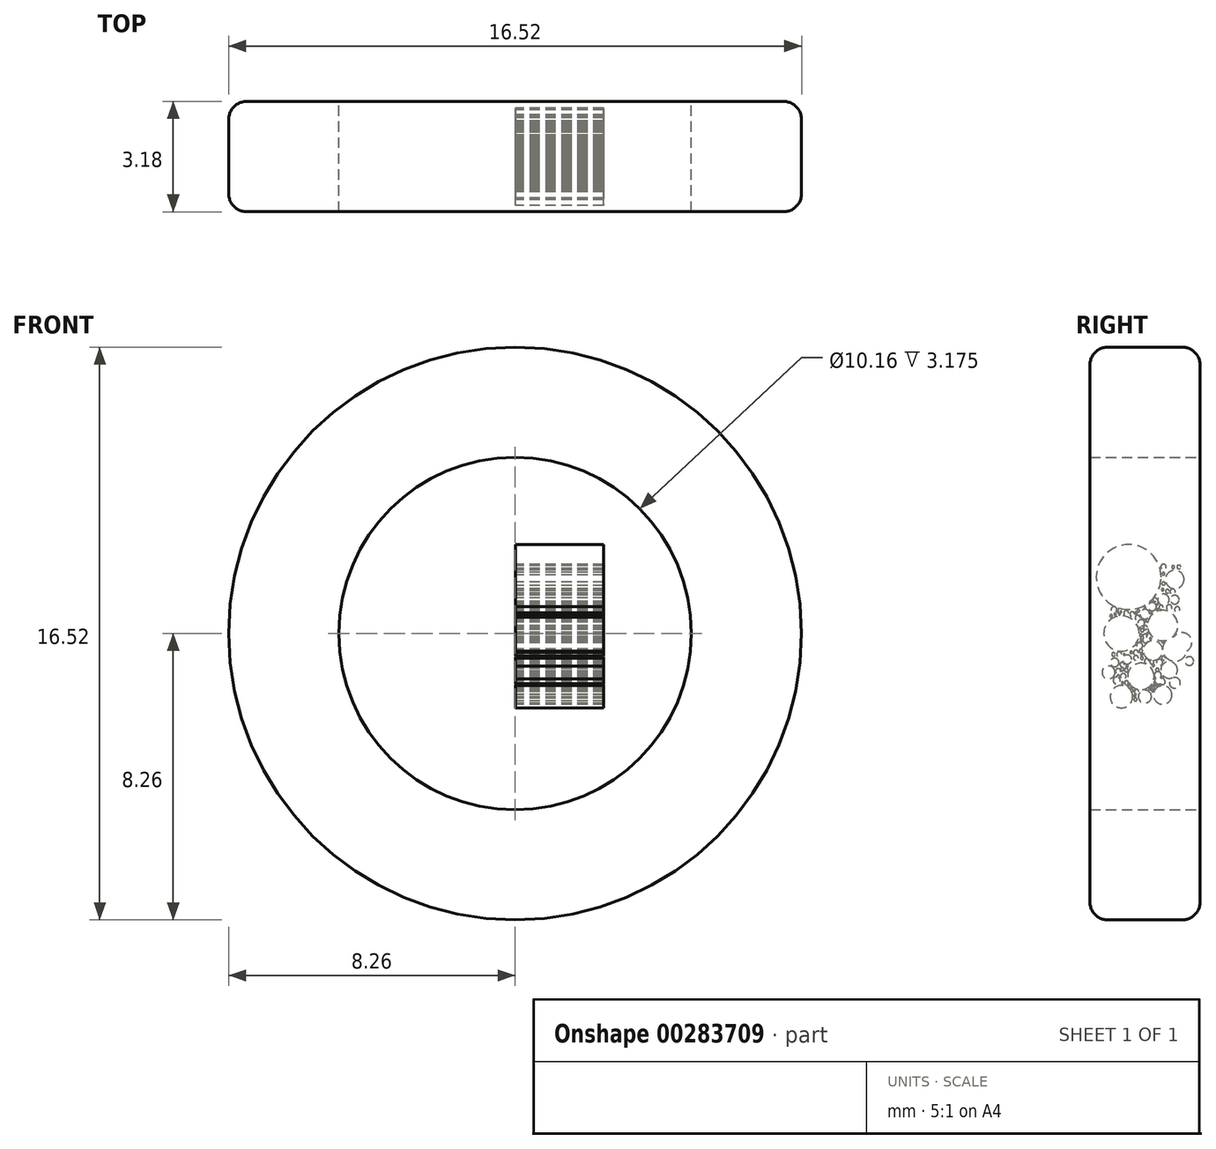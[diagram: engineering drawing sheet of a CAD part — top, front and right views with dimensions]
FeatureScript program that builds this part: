
annotation { "Feature Type Name" : "Feature", "Feature Type Description" : "" }
export const myFeature = defineFeature(function(context is Context, id is Id, definition is map)
    precondition{}
    {
        {
            var Q0;
            Q0=qCreatedBy(makeId("Front.planeOp"),FACE);
            var sketch = newSketch(context, id + "F0", { "sketchPlane" : qUnion([Q0])});
            skCircle(sketch, "E0", {"center": v(0, 0) * mm, "radius": 5.08 * mm});
            skCircle(sketch, "E1", {"center": v(0, 0) * mm, "radius": 8.26 * mm});
            skSolve(sketch);
        }
        {
            var Q0;
            Q0=makeQuery(id+"F0.imprint","IMPRINT",FACE,{"disambiguationData":[TD([[makeQuery(id+"F0.imprint","IMPRINT",EDGE,{"derivedFrom":sQuery(id+"F0.wireOp",EDGE,"E0")}),-1.0]])]});
            extrude(context, id + "F1", {"entities" : qUnion([Q0]), "depth" : 3.17 * mm});
        }
        {
            var Q0;
            Q0=makeQuery(id+"F1.opExtrude","CAP_EDGE",EDGE,{"disambiguationData":[OSD([sQuery(id+"F0.wireOp",EDGE,"E1")])],"isStart":false});
            var Q1;
            Q1=makeQuery(id+"F1.opExtrude","SWEPT_FACE",FACE,{"disambiguationData":[OSD([sQuery(id+"F0.wireOp",EDGE,"E1")])]});
            fillet(context, id + "F2", {"entities" : qUnion([Q0, Q1]), "radius" : 0.5 * mm, "tangentPropagation" : true, "allowEdgeOverflow" : false});
        }
        {
            var Q0;
            Q0=qCreatedBy(makeId("Right.planeOp"),FACE);
            cPlane(context, id + "F3", {"entities" : qUnion([Q0]), "cplaneType" : CPlaneType.OFFSET, "offset" : .625 / 50.8 * mm, "width" : 152.4 * mm, "height" : 152.4 * mm});
        }
        {
            var Q0;
            Q0=qCreatedBy(id+"F3.planeOp",FACE);
            var sketch = newSketch(context, id + "F4", { "sketchPlane" : qUnion([Q0])});
            skCircle(sketch, "E2", {"center": v(-2.06, 1.63) * mm, "radius": 0.94 * mm});
            skCircle(sketch, "E3", {"center": v(-1.7, -1.24) * mm, "radius": 0.38 * mm});
            skCircle(sketch, "E4", {"center": v(-1.08, 0.23) * mm, "radius": 0.44 * mm});
            skCircle(sketch, "E5", {"center": v(-0.73, 1.56) * mm, "radius": 0.27 * mm});
            skCircle(sketch, "E6", {"center": v(-2.27, 0) * mm, "radius": 0.51 * mm});
            skCircle(sketch, "E7", {"center": v(-2.64, -1.12) * mm, "radius": 0.19 * mm});
            skCircle(sketch, "E8", {"center": v(-0.9, -1.05) * mm, "radius": 0.24 * mm});
            skCircle(sketch, "E9", {"center": v(-1.08, -1.77) * mm, "radius": 0.27 * mm});
            skCircle(sketch, "E10", {"center": v(-2.27, -1.82) * mm, "radius": 0.32 * mm});
            skCircle(sketch, "E11", {"center": v(-1.05, 0.98) * mm, "radius": 0.16 * mm});
            skCircle(sketch, "E12", {"center": v(-0.73, 0.98) * mm, "radius": 0.13 * mm});
            skCircle(sketch, "E13", {"center": v(-1.36, -0.5) * mm, "radius": 0.28 * mm});
            skCircle(sketch, "E14", {"center": v(-0.52, -0.26) * mm, "radius": 0.28 * mm});
            skCircle(sketch, "E15", {"center": v(-0.73, -1.42) * mm, "radius": 0.16 * mm});
            skCircle(sketch, "E16", {"center": v(-0.3, -0.8) * mm, "radius": 0.13 * mm});
            skCircle(sketch, "E17", {"center": v(-0.73, -0.45) * mm, "radius": 0.35 * mm});
            skCircle(sketch, "E18", {"center": v(-2.1, -0.75) * mm, "radius": 0.13 * mm});
            skCircle(sketch, "E19", {"center": v(-1.59, -1.82) * mm, "radius": 0.19 * mm});
            skCircle(sketch, "E20", {"center": v(-1.59, 0.56) * mm, "radius": 0.14 * mm});
            skCircle(sketch, "E21", {"center": v(-1.05, 1.92) * mm, "radius": 0.08 * mm});
            skCircle(sketch, "E22", {"center": v(-0.77, 1.92) * mm, "radius": 0.04 * mm});
            skCircle(sketch, "E23", {"center": v(-0.61, 1.92) * mm, "radius": 0.06 * mm});
            skCircle(sketch, "E24", {"center": v(-1.05, 1.72) * mm, "radius": 0.04 * mm});
            skCircle(sketch, "E25", {"center": v(-1.05, 1.44) * mm, "radius": 0.05 * mm});
            skCircle(sketch, "E26", {"center": v(-0.94, 1.22) * mm, "radius": 0.05 * mm});
            skCircle(sketch, "E27", {"center": v(-0.8, 1.2) * mm, "radius": 0.08 * mm});
            skCircle(sketch, "E28", {"center": v(-1.38, 0.77) * mm, "radius": 0.12 * mm});
            skCircle(sketch, "E29", {"center": v(-0.66, 0.7) * mm, "radius": 0.08 * mm});
            skCircle(sketch, "E30", {"center": v(-0.9, 0.75) * mm, "radius": 0.08 * mm});
            skCircle(sketch, "E31", {"center": v(-1.96, 0.56) * mm, "radius": 0.07 * mm});
            skCircle(sketch, "E32", {"center": v(-1.08, 1.26) * mm, "radius": 0.04 * mm});
            skCircle(sketch, "E33", {"center": v(-1.7, 0.3) * mm, "radius": 0.1 * mm});
            skCircle(sketch, "E34", {"center": v(-1.66, 0.1) * mm, "radius": 0.05 * mm});
            skCircle(sketch, "E35", {"center": v(-1.59, -0.08) * mm, "radius": 0.06 * mm});
            skCircle(sketch, "E36", {"center": v(-1.52, 0) * mm, "radius": 0.03 * mm});
            skCircle(sketch, "E37", {"center": v(-1.57, 0.17) * mm, "radius": 0.06 * mm});
            skCircle(sketch, "E38", {"center": v(-1.57, 0.36) * mm, "radius": 0.03 * mm});
            skCircle(sketch, "E39", {"center": v(-1.73, 0.16) * mm, "radius": 0.02 * mm});
            skCircle(sketch, "E40", {"center": v(-1.85, 0.6) * mm, "radius": 0.04 * mm});
            skCircle(sketch, "E41", {"center": v(-1.8, 0.45) * mm, "radius": 0.07 * mm});
            skCircle(sketch, "E42", {"center": v(-1.59, 0.75) * mm, "radius": 0.02 * mm});
            skCircle(sketch, "E43", {"center": v(-1.4, 0.6) * mm, "radius": 0.03 * mm});
            skCircle(sketch, "E44", {"center": v(-1.13, 0.75) * mm, "radius": 0.06 * mm});
            skCircle(sketch, "E45", {"center": v(-1.3, 0.98) * mm, "radius": 0.05 * mm});
            skCircle(sketch, "E46", {"center": v(-1.22, 0.85) * mm, "radius": 0.02 * mm});
            skCircle(sketch, "E47", {"center": v(-1.24, 0.7) * mm, "radius": 0.03 * mm});
            skCircle(sketch, "E48", {"center": v(-2.13, 0.58) * mm, "radius": 0.07 * mm});
            skCircle(sketch, "E49", {"center": v(-2.28, 0.62) * mm, "radius": 0.02 * mm});
            skCircle(sketch, "E50", {"center": v(-2.32, 0.56) * mm, "radius": 0.02 * mm});
            skCircle(sketch, "E51", {"center": v(-2.48, 0.68) * mm, "radius": 0.09 * mm});
            skCircle(sketch, "E52", {"center": v(-2.56, 0.5) * mm, "radius": 0.04 * mm});
            skCircle(sketch, "E53", {"center": v(-2.45, 0.56) * mm, "radius": 0.03 * mm});
            skCircle(sketch, "E54", {"center": v(-2.37, 0.63) * mm, "radius": 0.02 * mm});
            skCircle(sketch, "E55", {"center": v(-2.35, 0.7) * mm, "radius": 0.01 * mm});
            skCircle(sketch, "E56", {"center": v(-1.78, 0.65) * mm, "radius": 0.04 * mm});
            skCircle(sketch, "E57", {"center": v(-1.74, -0.35) * mm, "radius": 0.09 * mm});
            skCircle(sketch, "E58", {"center": v(-1.85, -0.55) * mm, "radius": 0.07 * mm});
            skCircle(sketch, "E59", {"center": v(-1.7, -0.5) * mm, "radius": 0.05 * mm});
            skCircle(sketch, "E60", {"center": v(-1.57, -0.18) * mm, "radius": 0.08 * mm});
            skCircle(sketch, "E61", {"center": v(-1.7, -0.24) * mm, "radius": 0.03 * mm});
            skCircle(sketch, "E62", {"center": v(-1.7, -0.05) * mm, "radius": 0.04 * mm});
            skCircle(sketch, "E63", {"center": v(-1.7, -0.15) * mm, "radius": 0.02 * mm});
            skCircle(sketch, "E64", {"center": v(-1.43, -0.15) * mm, "radius": 0.03 * mm});
            skCircle(sketch, "E65", {"center": v(-1.08, -0.24) * mm, "radius": 0.03 * mm});
            skCircle(sketch, "E66", {"center": v(-1.05, -0.71) * mm, "radius": 0.06 * mm});
            skCircle(sketch, "E67", {"center": v(-1.17, -0.84) * mm, "radius": 0.1 * mm});
            skCircle(sketch, "E68", {"center": v(-1.35, -0.92) * mm, "radius": 0.03 * mm});
            skCircle(sketch, "E69", {"center": v(-1.39, -0.82) * mm, "radius": 0.06 * mm});
            skCircle(sketch, "E70", {"center": v(-1.54, -0.8) * mm, "radius": 0.07 * mm});
            skCircle(sketch, "E71", {"center": v(-1.67, -0.7) * mm, "radius": 0.04 * mm});
            skCircle(sketch, "E72", {"center": v(-1.68, -0.6) * mm, "radius": 0.03 * mm});
            skCircle(sketch, "E73", {"center": v(-1.85, -0.7) * mm, "radius": 0.07 * mm});
            skCircle(sketch, "E74", {"center": v(-1.99, -0.54) * mm, "radius": 0.03 * mm});
            skCircle(sketch, "E75", {"center": v(-2.19, -0.6) * mm, "radius": 0.02 * mm});
            skCircle(sketch, "E76", {"center": v(-2.33, -0.6) * mm, "radius": 0.07 * mm});
            skCircle(sketch, "E77", {"center": v(-2.46, -0.84) * mm, "radius": 0.12 * mm});
            skCircle(sketch, "E78", {"center": v(-2.5, -0.6) * mm, "radius": 0.05 * mm});
            skCircle(sketch, "E79", {"center": v(-2.24, -1.03) * mm, "radius": 0.05 * mm});
            skCircle(sketch, "E80", {"center": v(-2.25, -0.9) * mm, "radius": 0.06 * mm});
            skCircle(sketch, "E81", {"center": v(-2.1, -0.94) * mm, "radius": 0.04 * mm});
            skCircle(sketch, "E82", {"center": v(-1.23, -1.05) * mm, "radius": 0.05 * mm});
            skCircle(sketch, "E83", {"center": v(-1.22, -1.2) * mm, "radius": 0.1 * mm});
            skCircle(sketch, "E84", {"center": v(-1.08, -1.4) * mm, "radius": 0.08 * mm});
            skCircle(sketch, "E85", {"center": v(-1.2, -1.35) * mm, "radius": 0.1 * mm});
            skCircle(sketch, "E86", {"center": v(-1.31, -1.5) * mm, "radius": 0.04 * mm});
            skCircle(sketch, "E87", {"center": v(-1.32, -1.42) * mm, "radius": 0.02 * mm});
            skCircle(sketch, "E88", {"center": v(-1.18, -1.48) * mm, "radius": 0.03 * mm});
            skCircle(sketch, "E89", {"center": v(-1.07, -1.26) * mm, "radius": 0.02 * mm});
            skCircle(sketch, "E90", {"center": v(-1.25, -1.5) * mm, "radius": 0.01 * mm});
            skCircle(sketch, "E91", {"center": v(-1.4, -1.5) * mm, "radius": 0.02 * mm});
            skCircle(sketch, "E92", {"center": v(-1.35, -1.56) * mm, "radius": 0.04 * mm});
            skCircle(sketch, "E93", {"center": v(-1.43, -1.55) * mm, "radius": 0.02 * mm});
            skCircle(sketch, "E94", {"center": v(-1.37, -1.64) * mm, "radius": 0.04 * mm});
            skCircle(sketch, "E95", {"center": v(-1.43, -1.62) * mm, "radius": 0.01 * mm});
            skCircle(sketch, "E96", {"center": v(-1.48, -1.6) * mm, "radius": 0.01 * mm});
            skCircle(sketch, "E97", {"center": v(-1.47, -1.57) * mm, "radius": 0.01 * mm});
            skCircle(sketch, "E98", {"center": v(-1.86, -1.9) * mm, "radius": 0.04 * mm});
            skCircle(sketch, "E99", {"center": v(-1.88, -1.8) * mm, "radius": 0.03 * mm});
            skCircle(sketch, "E100", {"center": v(-1.83, -1.68) * mm, "radius": 0.07 * mm});
            skCircle(sketch, "E101", {"center": v(-1.93, -1.65) * mm, "radius": 0.02 * mm});
            skCircle(sketch, "E102", {"center": v(-1.98, -1.56) * mm, "radius": 0.03 * mm});
            skCircle(sketch, "E103", {"center": v(-2.07, -1.5) * mm, "radius": 0.03 * mm});
            skCircle(sketch, "E104", {"center": v(-2.12, -1.42) * mm, "radius": 0.06 * mm});
            skCircle(sketch, "E105", {"center": v(-2.21, -1.24) * mm, "radius": 0.08 * mm});
            skCircle(sketch, "E106", {"center": v(-2.4, -1.35) * mm, "radius": 0.1 * mm});
            skCircle(sketch, "E107", {"center": v(-2.24, -1.42) * mm, "radius": 0.03 * mm});
            skCircle(sketch, "E108", {"center": v(-2.13, -1.05) * mm, "radius": 0.05 * mm});
            skCircle(sketch, "E109", {"center": v(-2.36, -1.09) * mm, "radius": 0.08 * mm});
            skCircle(sketch, "E110", {"center": v(-2.36, -1.24) * mm, "radius": 0.04 * mm});
            skSolve(sketch);
        }
        {
            var Q0;
            Q0 = qSketchRegion(id + "F4", true);
            extrude(context, id + "F5", {"entities" : qUnion([Q0]), "depth" : 2.54 * mm});
        }
    });
